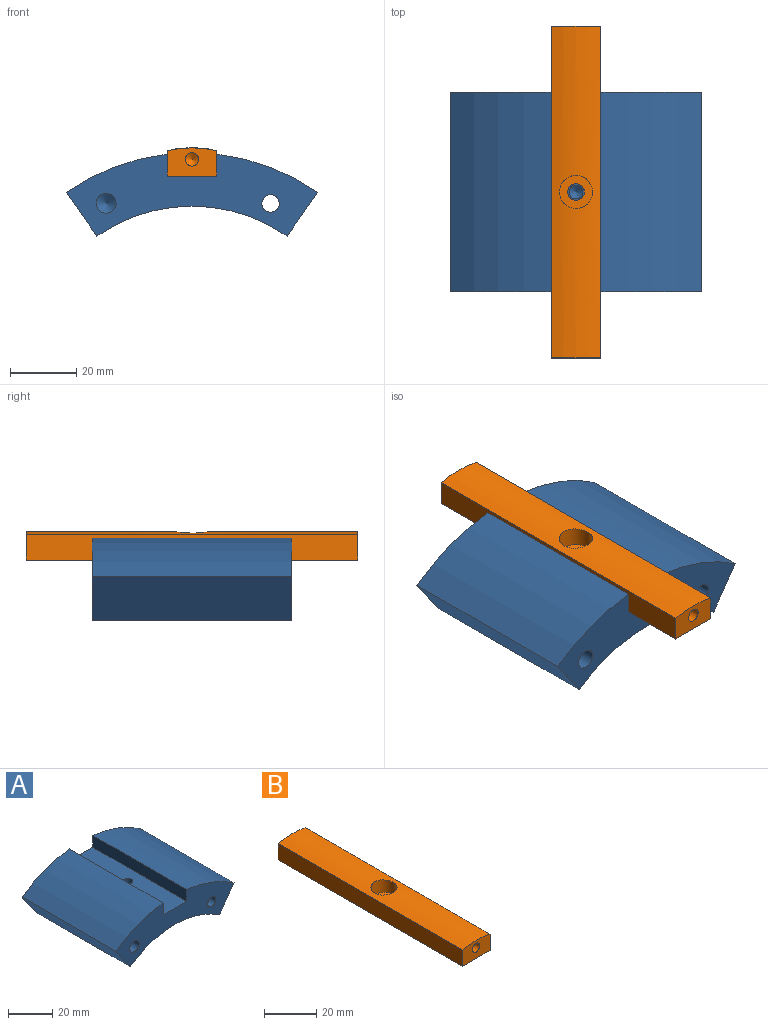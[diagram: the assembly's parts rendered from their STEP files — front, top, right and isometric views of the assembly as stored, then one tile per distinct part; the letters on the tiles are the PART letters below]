
ASSEMBLY  parts=2 mates=1
PART A: 27 faces, bbox 75.7x60x24.7 mm
  f0: cylinder r=49.92mm len=60mm, axis (0,1,0), area 3224.6mm2, adj f3,f4,f8,f9,f14,f15,f16,f18
  f1: plane 60x6.57mm, normal (1,0,0), area 394.3mm2, adj f2,f7,f8,f9
  f2: cylinder r=66mm len=60mm, axis (0,1,0), area 1968.1mm2, adj f1,f3,f8,f9
  f3: plane 60x13.17mm, normal (-0.82,0,-0.57), area 964.6mm2, adj f0,f2,f8,f9
  f4: plane 60x13.17mm, normal (0.82,0,-0.57), area 964.6mm2, adj f0,f5,f8,f9
  f5: cylinder r=66mm len=60mm, axis (0,1,0), area 1968.1mm2, adj f4,f6,f8,f9
  f6: plane 60x6.57mm, normal (-1,0,0), area 394.3mm2, adj f5,f7,f8,f9
  f7: plane 60x15mm, normal (0,0,1), area 886.1mm2, adj f1,f6,f8,f9,f13
  f8: plane 75.71x24.68mm, normal (0,-1,0), area 985.7mm2, adj f0,f1,f2,f3,f4,f5,f6,f7
  f9: plane 75.71x24.68mm, normal (0,1,0), area 1014mm2, adj f0,f1,f2,f3,f4,f5,f6,f7
  f10: cone r=0mm half-angle=59deg, axis (0,-1,0), area 33mm2, adj f11
  f11: cylinder r=3mm len=35mm, axis (0,-1,0), area 659.7mm2, adj f8,f10
  f12: cone r=0mm half-angle=59deg, axis (0,0,1), area 16.2mm2, adj f13
  f13: cylinder r=2.1mm len=4.8mm, axis (0,0,1), area 63.3mm2, adj f7,f12
  f14: plane 49.01x0.12mm, normal (0.42,0,0.91), area 6.6mm2, adj f0,f20,f21,f22
  f15: plane 13.71x11.24mm, normal (0,-1,0), area 59.5mm2, adj f0,f16,f22,f23,f26
  f16: cylinder r=1mm len=11.3mm, axis (-0.42,0,-0.91), area 18.8mm2, adj f0,f15,f17,f23,f24
  f17: plane 48x10.88mm, normal (0.91,0,-0.42), area 576mm2, adj f16,f18,f23,f24
  f18: cylinder r=1mm len=11.3mm, axis (-0.42,0,-0.91), area 18.8mm2, adj f0,f17,f19,f23,f24
  f19: plane 13.71x11.24mm, normal (0,1,0), area 59.5mm2, adj f0,f18,f20,f23,f25
  f20: cylinder r=1mm len=11.3mm, axis (-0.42,0,-0.91), area 18.8mm2, adj f0,f14,f19,f21,f23
  f21: plane 48x10.88mm, normal (-0.91,0,0.42), area 576mm2, adj f14,f20,f22,f23
  f22: cylinder r=1mm len=11.3mm, axis (-0.42,0,-0.91), area 18.8mm2, adj f0,f14,f15,f21,f23
  f23: plane 50x8.02mm, normal (-0.42,0,-0.91), area 441.5mm2, adj f15,f16,f17,f18,f19,f20,f21,f22
  f24: plane 48.26x0.01mm, normal (0.42,0,0.91), area 0.4mm2, adj f0,f16,f17,f18
  f25: cylinder r=2.62mm len=5.25mm, axis (0,-1,0), area 82.5mm2, adj f8,f19
  f26: cylinder r=2.62mm len=5.25mm, axis (0,-1,0), area 82.5mm2, adj f9,f15
PART B: 13 faces, bbox 15x100x8.5 mm
  f0: cylinder r=35mm len=100mm, axis (0,1,0), area 1433mm2, adj f2,f3,f4,f5,f6
  f1: plane 100x15mm, normal (0,0,-1), area 1480.4mm2, adj f2,f3,f4,f5,f8
  f2: plane 100x7.69mm, normal (1,0,0), area 768.7mm2, adj f0,f1,f4,f5
  f3: plane 100x7.69mm, normal (-1,0,0), area 768.7mm2, adj f0,f1,f4,f5
  f4: plane 15x8.5mm, normal (0,-1,0), area 110.9mm2, adj f0,f1,f2,f3,f9
  f5: plane 15x8.5mm, normal (0,1,0), area 110.9mm2, adj f0,f1,f2,f3,f11
  f6: cylinder r=5mm len=10mm, axis (0,0,1), area 182.9mm2, adj f0,f7
  f7: plane 10x10mm, normal (0,0,1), area 58.9mm2, adj f6,f8
  f8: cylinder r=2.5mm len=5mm, axis (0,0,1), area 39.3mm2, adj f1,f7
  f9: cylinder r=2mm len=10mm, axis (0,-1,0), area 125.7mm2, adj f4,f10
  f10: cone r=0mm half-angle=59deg, axis (0,-1,0), area 14.7mm2, adj f9
  f11: cylinder r=2mm len=10mm, axis (0,1,0), area 125.7mm2, adj f5,f12
  f12: cone r=0mm half-angle=59deg, axis (0,1,0), area 14.7mm2, adj f11
PLACE A t=(-54.98,136.91,25.52)mm
PLACE B t=(-62.48,156.91,84.52)mm
MATE fastened A.f12 <-> B.f6  axis (0,0,1) through (-54.98,106.91,84.52)mm
